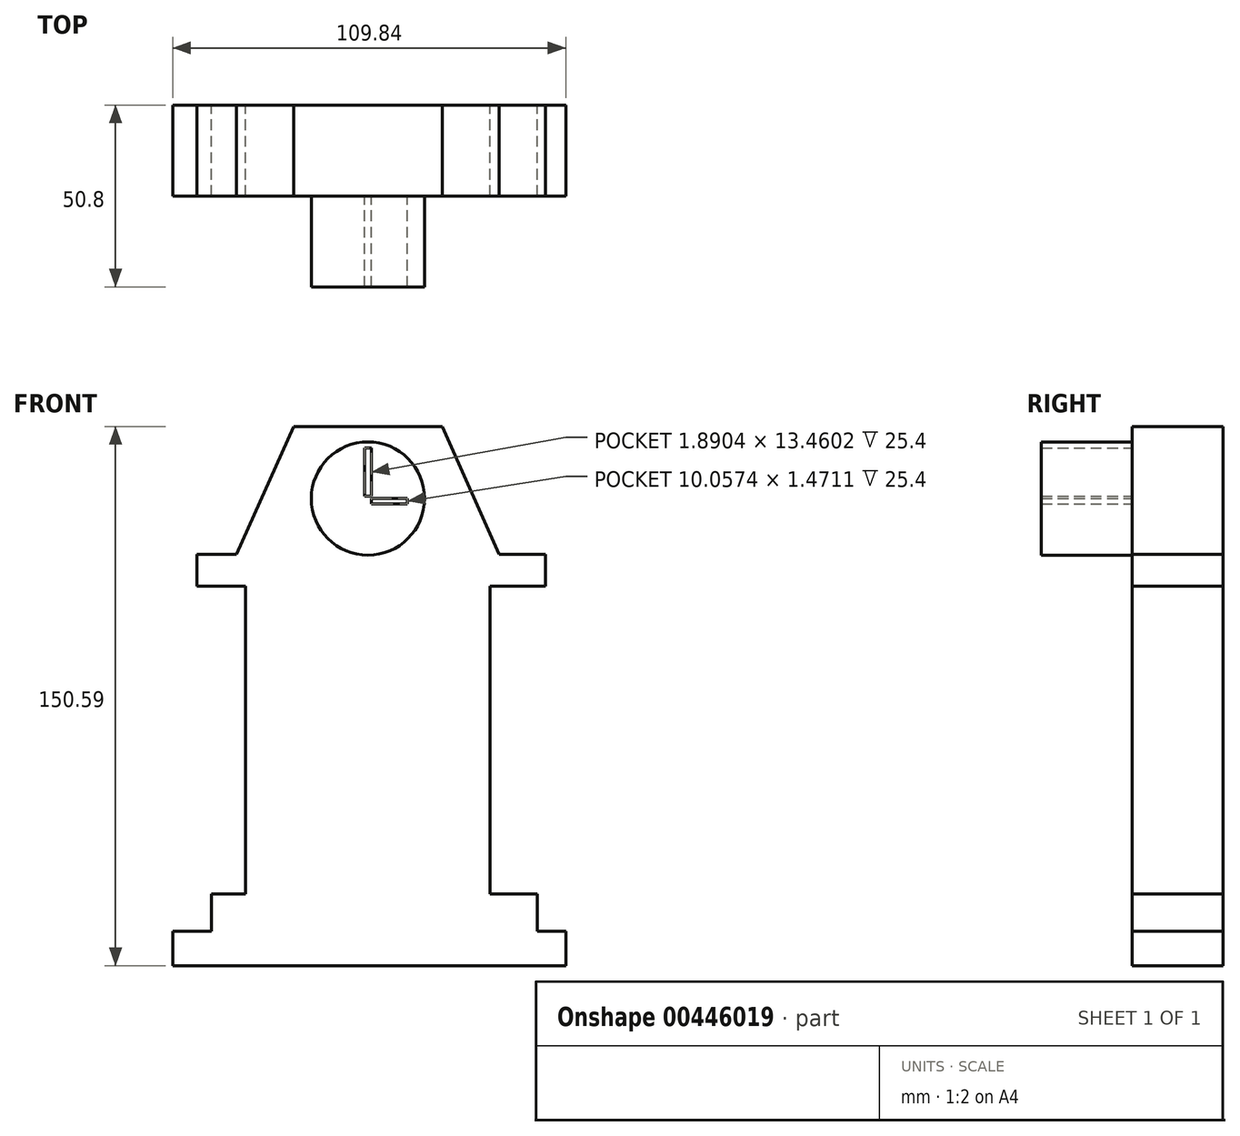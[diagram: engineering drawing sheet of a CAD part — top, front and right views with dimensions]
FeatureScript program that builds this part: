
annotation { "Feature Type Name" : "Feature", "Feature Type Description" : "" }
export const myFeature = defineFeature(function(context is Context, id is Id, definition is map)
    precondition{}
    {
        {
            var Q0;
            Q0=qCreatedBy(makeId("Front.planeOp"),FACE);
            var sketch = newSketch(context, id + "F0", { "sketchPlane" : qUnion([Q0])});
            skLineSegment(sketch, "E0.bottom", {"start": v(-54.54, -66.86) * mm, "end": v(55.3, -66.86) * mm});
            skLineSegment(sketch, "E0.top", {"start": v(-54.54, -76.41) * mm, "end": v(55.3, -76.41) * mm});
            skLineSegment(sketch, "E0.left", {"start": v(-54.54, -66.86) * mm, "end": v(-54.54, -76.41) * mm});
            skLineSegment(sketch, "E0.right", {"start": v(55.3, -66.86) * mm, "end": v(55.3, -76.41) * mm});
            skLineSegment(sketch, "E1.bottom", {"start": v(-43.71, -66.86) * mm, "end": v(47.34, -66.86) * mm});
            skLineSegment(sketch, "E1.top", {"start": v(-43.71, -56.35) * mm, "end": v(47.34, -56.35) * mm});
            skLineSegment(sketch, "E1.left", {"start": v(-43.71, -66.86) * mm, "end": v(-43.71, -56.35) * mm});
            skLineSegment(sketch, "E1.right", {"start": v(47.34, -66.86) * mm, "end": v(47.34, -56.35) * mm});
            skLineSegment(sketch, "E2", {"start": v(-34.16, -56.35) * mm, "end": v(-34.16, 30.24) * mm});
            skLineSegment(sketch, "E3.MirrorCS", {"start": v(34.16, -56.35) * mm, "end": v(34.16, 30.24) * mm});
            skLineSegment(sketch, "E4", {"start": v(-34.16, 30.24) * mm, "end": v(34.16, 30.24) * mm});
            skLineSegment(sketch, "E5.bottom", {"start": v(-47.85, 38.52) * mm, "end": v(49.57, 38.52) * mm});
            skLineSegment(sketch, "E5.top", {"start": v(-47.85, 29.6) * mm, "end": v(49.57, 29.6) * mm});
            skLineSegment(sketch, "E5.left", {"start": v(-47.85, 38.52) * mm, "end": v(-47.85, 29.6) * mm});
            skLineSegment(sketch, "E5.right", {"start": v(49.57, 38.52) * mm, "end": v(49.57, 29.6) * mm});
            skLineSegment(sketch, "E6", {"start": v(-36.71, 38.52) * mm, "end": v(-20.8, 74.18) * mm});
            skLineSegment(sketch, "E7.MirrorCS", {"start": v(36.71, 38.52) * mm, "end": v(20.8, 74.18) * mm});
            skLineSegment(sketch, "E8", {"start": v(-20.8, 74.18) * mm, "end": v(20.8, 74.18) * mm});
            skSolve(sketch);
        }
        {
            var Q0;
            Q0 = qSketchRegion(id + "F0", true);
            extrude(context, id + "F1", {"entities" : qUnion([Q0]), "depth" : 25.4 * mm});
        }
        {
            var Q0;
            Q0=makeQuery(id+"F1.opExtrude","CAP_FACE",FACE,{"disambiguationData":[OSD([sQuery(id+"F0.wireOp",EDGE,"E0.bottom"),sQuery(id+"F0.wireOp",EDGE,"E0.top"),sQuery(id+"F0.wireOp",EDGE,"E0.left"),sQuery(id+"F0.wireOp",EDGE,"E0.right"),sQuery(id+"F0.wireOp",EDGE,"E1.top"),sQuery(id+"F0.wireOp",EDGE,"E1.left"),sQuery(id+"F0.wireOp",EDGE,"E1.right"),sQuery(id+"F0.wireOp",EDGE,"E2"),sQuery(id+"F0.wireOp",EDGE,"E3.MirrorCS"),sQuery(id+"F0.wireOp",EDGE,"E5.bottom"),sQuery(id+"F0.wireOp",EDGE,"E5.top"),sQuery(id+"F0.wireOp",EDGE,"E5.left"),sQuery(id+"F0.wireOp",EDGE,"E5.right"),sQuery(id+"F0.wireOp",EDGE,"E6"),sQuery(id+"F0.wireOp",EDGE,"E7.MirrorCS"),sQuery(id+"F0.wireOp",EDGE,"E8")])],"isStart":false});
            var sketch = newSketch(context, id + "F2", { "sketchPlane" : qUnion([Q0])});
            skCircle(sketch, "E9", {"center": v(0, 54.07) * mm, "radius": 15.82 * mm});
            skLineSegment(sketch, "E10", {"start": v(-0.95, 54.72) * mm, "end": v(-0.95, 68.18) * mm});
            skLineSegment(sketch, "E11", {"start": v(-0.95, 68.18) * mm, "end": v(0.94, 68.18) * mm});
            skLineSegment(sketch, "E12", {"start": v(0.94, 68.18) * mm, "end": v(0.94, 54.8) * mm});
            skLineSegment(sketch, "E13", {"start": v(0.94, 54.8) * mm, "end": v(-0.95, 54.72) * mm});
            skLineSegment(sketch, "E14", {"start": v(0.94, 54.07) * mm, "end": v(0.94, 52.6) * mm});
            skLineSegment(sketch, "E15", {"start": v(0.94, 52.6) * mm, "end": v(11, 52.6) * mm});
            skLineSegment(sketch, "E16", {"start": v(11, 52.6) * mm, "end": v(11, 54.07) * mm});
            skLineSegment(sketch, "E17", {"start": v(11, 54.07) * mm, "end": v(0.94, 54.07) * mm});
            skSolve(sketch);
        }
        {
            var Q0;
            Q0 = qSketchRegion(id + "F2", true);
            extrude(context, id + "F3", {"entities" : qUnion([Q0]), "operationType" : NewBodyOperationType.ADD, "depth" : 25.4 * mm});
        }
    });
